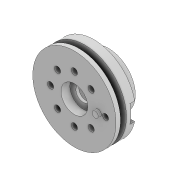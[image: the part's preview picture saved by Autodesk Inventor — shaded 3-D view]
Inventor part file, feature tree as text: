
AUTODESK INVENTOR PART (.ipt)
format: ipt  version: 2022 (Build 260153000, 153)  size: 256,000 bytes
history: native  units: mm
features: extrude x9, sketch x9, projected_geometry x4, revolve x1, pattern_circular x1
ambient origin geometry x8: Origin, YZ Plane, XZ Plane, XY Plane, X Axis, Y Axis, Z Axis, Center Point
bodies: Solid1 (feature_tree)
feature tree (24):
  revolve  "Revolution1"  [1 undecoded]
  extrude  "Extrusion1"  Depth=1.5mm
  pattern_circular  "Circular Pattern1"  Count=10  [1 undecoded]
  extrude  "Extrusion2"  Depth=2.0mm
  extrude  "Extrusion3"  Depth=0.5mm TaperAngle=0.0deg
  extrude  "Extrusion8"  Depth=4.0mm
  extrude  "Extrusion6"  Depth=5.0mm TaperAngle=0.0deg
  extrude  "Extrusion7"  Depth=0.5mm
  sketch  "Sketch11"  dims[d16=10.5mm d17=100.0mm d18=0.0mm d19=4.0mm d20=5.0mm d21=0.0mm d24=10.25mm d25=2.0mm d26=0.0mm d31=2.0mm d32=4.0mm d33=0.0mm d34=18.0mm d35=1.5mm d36=0.0mm d37=5.0mm d38=1.0mm d39=0.0mm d40=100.0mm d41=0.0mm d44=4.0mm d45=4.0mm d46=4.0mm d47=4.0mm d48=4.0mm d49=4.0mm d50=4.0mm d51=3.0mm d52=3.0mm d53=3.0mm d54=1.6mm d55=0.0mm d56=6.0mm d57=0.0mm d42=0.5mm d43=0.872665mm]
  extrude  "Extrusion10"  Depth=2.0mm TaperAngle=0.0deg
  extrude  "Extrusion11"  Depth=2.0mm
  extrude  "Extrusion9"  Depth=4.0mm TaperAngle=0.0deg
  sketch  "Sketch1"  dims[d0=5.0mm d1=3.0mm]
  sketch  "Sketch2"  dims[d2=14.0mm d4=1.5mm]
  sketch  "Sketch3"  dims[d5=1.5mm]
  sketch  "Sketch4"  dims[d6=360.0deg]
  projected_geometry  "Projected Loop1"
  projected_geometry  "Projected Loop2"
  sketch  "Sketch7"  dims[d7=2.1mm]
  sketch  "Sketch8"  dims[d8=8.0mm]
  projected_geometry  "Projected Loop5"
  sketch  "Sketch9"  dims[d9=9.0mm d10=100.0mm d11=0.0mm]
  sketch  "Sketch10"  dims[d12=80.0mm d13=360.0deg d15=2.0mm]
  projected_geometry  "Project Cut Edges1"
note: 2 required parameter values undecoded (feature->parameter linkage not recoverable at this tier; creation-order binding heuristic only, values carry confidence <= 0.55)